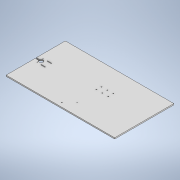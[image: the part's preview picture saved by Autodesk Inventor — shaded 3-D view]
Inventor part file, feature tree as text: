
AUTODESK INVENTOR PART (.ipt)
format: ipt  version: 2021.1 (Build 251245010, 245A)  size: 222,720 bytes
history: native  units: mm
features: extrude x4, sketch x4, other x1
ambient origin geometry x8: Origin, YZ Plane, XZ Plane, XY Plane, X Axis, Y Axis, Z Axis, Center Point
bodies: Body1 (feature_tree)
feature tree (9):
  other  "Твердое тело1"
  extrude  "Выдавливание1"  Depth=275.0mm
  extrude  "Выдавливание2"  Depth=150.0mm
  extrude  "Выдавливание3"  Depth=6.0mm TaperAngle=0.0deg
  extrude  "Выдавливание4"  TaperAngle=135.0deg  [1 undecoded]
  sketch  "Эскиз1"
  sketch  "Эскиз2"
  sketch  "Эскиз3"
  sketch  "Эскиз4"
note: 1 required parameter value undecoded (feature->parameter linkage not recoverable at this tier; creation-order binding heuristic only, values carry confidence <= 0.55)
